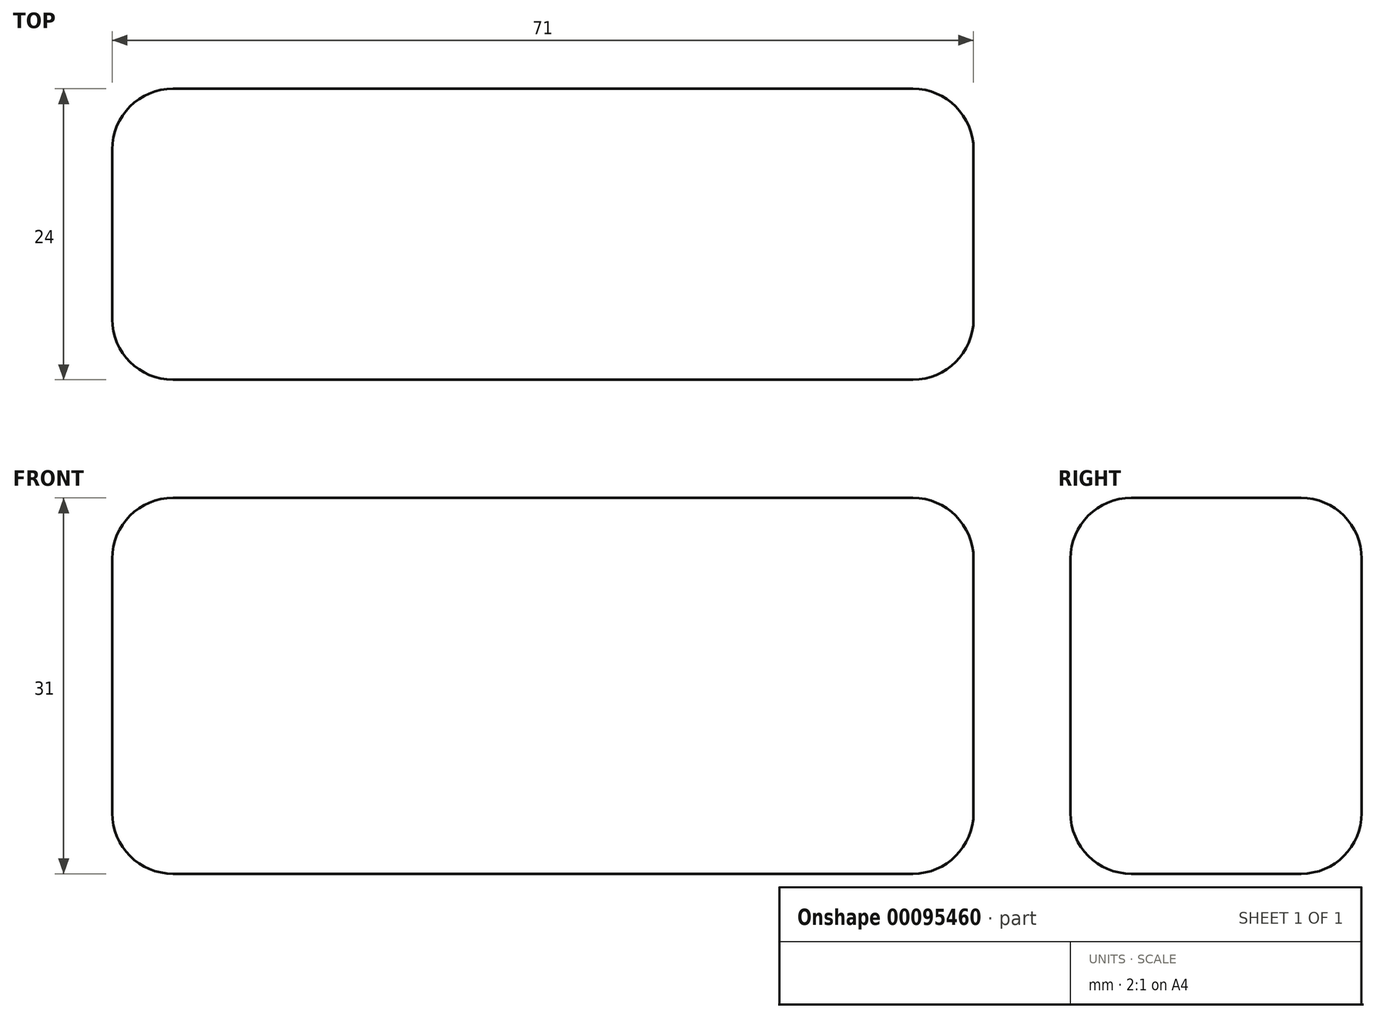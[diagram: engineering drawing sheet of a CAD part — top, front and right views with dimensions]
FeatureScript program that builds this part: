
annotation { "Feature Type Name" : "Feature", "Feature Type Description" : "" }
export const myFeature = defineFeature(function(context is Context, id is Id, definition is map)
    precondition{}
    {
        {
            var Q0;
            Q0=qCreatedBy(makeId("Front.planeOp"),FACE);
            var sketch = newSketch(context, id + "F0", { "sketchPlane" : qUnion([Q0])});
            skLineSegment(sketch, "E0.bottom", {"start": v(-35.5, 15.5) * mm, "end": v(35.5, 15.5) * mm});
            skLineSegment(sketch, "E0.top", {"start": v(-35.5, -15.5) * mm, "end": v(35.5, -15.5) * mm});
            skLineSegment(sketch, "E0.left", {"start": v(-35.5, 15.5) * mm, "end": v(-35.5, -15.5) * mm});
            skLineSegment(sketch, "E0.right", {"start": v(35.5, 15.5) * mm, "end": v(35.5, -15.5) * mm});
            skPoint(sketch, "E0.middle", {"position": v(0, 0) * mm});
            skSolve(sketch);
        }
        {
            var Q0;
            Q0 = qSketchRegion(id + "F0", true);
            extrude(context, id + "F1", {"entities" : qUnion([Q0]), "endBound" : BoundingType.SYMMETRIC, "depth" : 24 * mm});
        }
        {
            var Q0;
            Q0=makeQuery(id+"F1.opExtrude","SWEPT_FACE",FACE,{"disambiguationData":[OSD([sQuery(id+"F0.wireOp",EDGE,"E0.bottom")])]});
            var Q1;
            Q1=makeQuery(id+"F1.opExtrude","CAP_FACE",FACE,{"disambiguationData":[OSD([sQuery(id+"F0.wireOp",EDGE,"E0.bottom"),sQuery(id+"F0.wireOp",EDGE,"E0.top"),sQuery(id+"F0.wireOp",EDGE,"E0.left"),sQuery(id+"F0.wireOp",EDGE,"E0.right")])],"isStart":false});
            var Q2;
            Q2=makeQuery(id+"F1.opExtrude","SWEPT_FACE",FACE,{"disambiguationData":[OSD([sQuery(id+"F0.wireOp",EDGE,"E0.right")])]});
            var Q3;
            Q3=makeQuery(id+"F1.opExtrude","SWEPT_FACE",FACE,{"disambiguationData":[OSD([sQuery(id+"F0.wireOp",EDGE,"E0.left")])]});
            var Q4;
            Q4=makeQuery(id+"F1.opExtrude","CAP_FACE",FACE,{"disambiguationData":[OSD([sQuery(id+"F0.wireOp",EDGE,"E0.bottom"),sQuery(id+"F0.wireOp",EDGE,"E0.top"),sQuery(id+"F0.wireOp",EDGE,"E0.left"),sQuery(id+"F0.wireOp",EDGE,"E0.right")])],"isStart":true});
            var Q5;
            Q5=makeQuery(id+"F1.opExtrude","SWEPT_FACE",FACE,{"disambiguationData":[OSD([sQuery(id+"F0.wireOp",EDGE,"E0.top")])]});
            fillet(context, id + "F2", {"entities" : qUnion([Q0, Q1, Q2, Q3, Q4, Q5]), "radius" : 5 * mm, "tangentPropagation" : true, "allowEdgeOverflow" : false});
        }
    });
